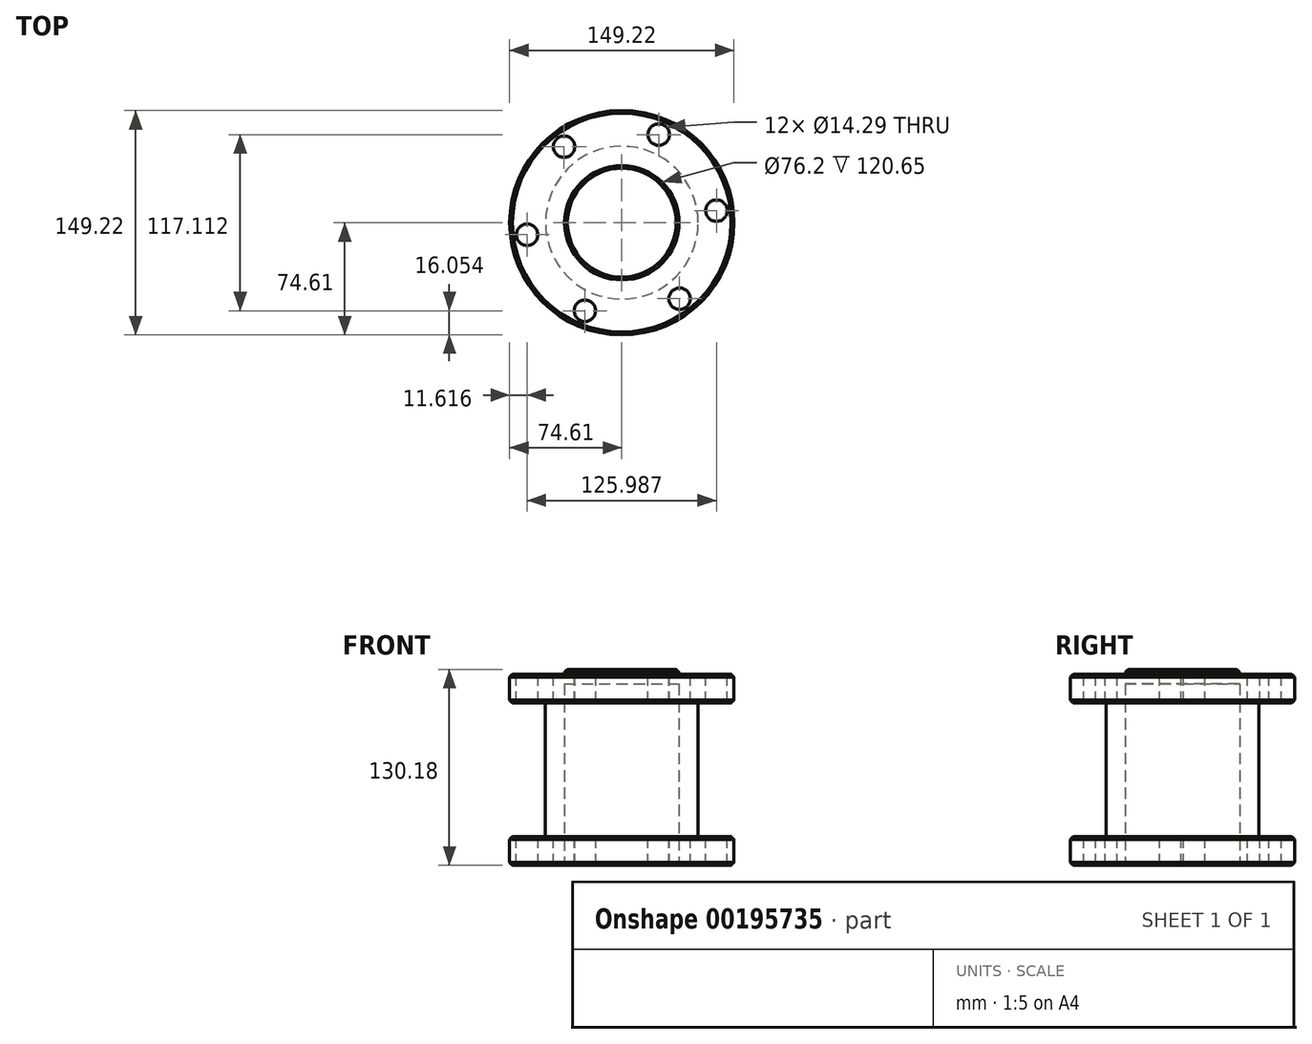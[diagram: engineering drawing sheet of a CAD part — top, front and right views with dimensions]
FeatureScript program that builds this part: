
annotation { "Feature Type Name" : "Feature", "Feature Type Description" : "" }
export const myFeature = defineFeature(function(context is Context, id is Id, definition is map)
    precondition{}
    {
        {
            var Q0;
            Q0=qCreatedBy(makeId("Top.planeOp"),FACE);
            var sketch = newSketch(context, id + "F0", { "sketchPlane" : qUnion([Q0])});
            skCircle(sketch, "E0", {"center": v(0, 0) * mm, "radius": 74.61 * mm});
            skSolve(sketch);
        }
        {
            var Q0;
            Q0 = qSketchRegion(id + "F0", true);
            extrude(context, id + "F1", {"entities" : qUnion([Q0]), "depth" : 19.05 * mm, "offsetDistance" : 25.4 * mm});
        }
        {
            var Q0;
            Q0=makeQuery(id+"F1.opExtrude","CAP_FACE",FACE,{"disambiguationData":[OSD([sQuery(id+"F0.wireOp",EDGE,"E0")])],"isStart":false});
            var sketch = newSketch(context, id + "F2", { "sketchPlane" : qUnion([Q0])});
            skCircle(sketch, "E1", {"center": v(0, 0) * mm, "radius": 50.8 * mm});
            skSolve(sketch);
        }
        {
            var Q0;
            Q0 = qSketchRegion(id + "F2", true);
            extrude(context, id + "F3", {"entities" : qUnion([Q0]), "operationType" : NewBodyOperationType.ADD, "depth" : 88.9 * mm, "offsetDistance" : 25.4 * mm});
        }
        {
            var Q0;
            Q0=makeQuery(id+"F3.opExtrude","CAP_FACE",FACE,{"disambiguationData":[OSD([sQuery(id+"F2.wireOp",EDGE,"E1")])],"isStart":false});
            var sketch = newSketch(context, id + "F4", { "sketchPlane" : qUnion([Q0])});
            skCircle(sketch, "E2", {"center": v(0, 0) * mm, "radius": 74.61 * mm});
            skSolve(sketch);
        }
        {
            var Q0;
            Q0 = qSketchRegion(id + "F4", true);
            extrude(context, id + "F5", {"entities" : qUnion([Q0]), "operationType" : NewBodyOperationType.ADD, "depth" : 19.05 * mm, "offsetDistance" : 25.4 * mm});
        }
        {
            var Q0;
            Q0=makeQuery(id+"F5.opExtrude","CAP_FACE",FACE,{"disambiguationData":[OSD([sQuery(id+"F4.wireOp",EDGE,"E2")])],"isStart":false});
            var sketch = newSketch(context, id + "F6", { "sketchPlane" : qUnion([Q0])});
            skCircle(sketch, "E3", {"center": v(0, 0) * mm, "radius": 63.5 * mm, "construction": true});
            skCircle(sketch, "E4", {"center": v(24.57, 58.56) * mm, "radius": 7.14 * mm});
            skCircle(sketch, "E5.1.0", {"center": v(-38.43, 50.55) * mm, "radius": 7.14 * mm});
            skCircle(sketch, "E5.2.0", {"center": v(-63, -8) * mm, "radius": 7.14 * mm});
            skCircle(sketch, "E5.3.0", {"center": v(-24.57, -58.56) * mm, "radius": 7.14 * mm});
            skCircle(sketch, "E5.4.0", {"center": v(38.43, -50.55) * mm, "radius": 7.14 * mm});
            skCircle(sketch, "E5.5.0", {"center": v(63, 8) * mm, "radius": 7.14 * mm});
            skSolve(sketch);
        }
        {
            var Q0;
            Q0 = qSketchRegion(id + "F6", true);
            extrude(context, id + "F7", {"entities" : qUnion([Q0]), "operationType" : NewBodyOperationType.REMOVE, "endBound" : BoundingType.THROUGH_ALL, "oppositeDirection" : true, "depth" : 25.4 * mm, "offsetDistance" : 25.4 * mm});
        }
        {
            var Q0;
            Q0=makeQuery(id+"F5.opExtrude","CAP_FACE",FACE,{"disambiguationData":[OSD([sQuery(id+"F4.wireOp",EDGE,"E2")])],"isStart":false});
            var sketch = newSketch(context, id + "F8", { "sketchPlane" : qUnion([Q0])});
            skCircle(sketch, "E6", {"center": v(0, 0) * mm, "radius": 38.1 * mm});
            skSolve(sketch);
        }
        {
            var Q0;
            Q0 = qSketchRegion(id + "F8", true);
            extrude(context, id + "F9", {"entities" : qUnion([Q0]), "operationType" : NewBodyOperationType.ADD, "depth" : 3.17 * mm, "offsetDistance" : 25.4 * mm});
        }
        {
            var Q0;
            Q0=makeQuery(id+"F1.opExtrude","CAP_FACE",FACE,{"disambiguationData":[OSD([sQuery(id+"F0.wireOp",EDGE,"E0")])],"isStart":true});
            var sketch = newSketch(context, id + "F10", { "sketchPlane" : qUnion([Q0])});
            skCircle(sketch, "E7", {"center": v(0, 0) * mm, "radius": 38.1 * mm});
            skSolve(sketch);
        }
        {
            var Q0;
            Q0 = qSketchRegion(id + "F10", true);
            extrude(context, id + "F11", {"entities" : qUnion([Q0]), "operationType" : NewBodyOperationType.REMOVE, "oppositeDirection" : true, "depth" : 120.65 * mm, "offsetDistance" : 25.4 * mm});
        }
        {
            var Q0;
            Q0=makeQuery(id+"F1.opExtrude","CAP_EDGE",EDGE,{"disambiguationData":[OSD([sQuery(id+"F0.wireOp",EDGE,"E0")])],"isStart":true});
            var Q1;
            Q1=makeQuery(id+"F11.boolean.opBoolean","COPY",EDGE,{"derivedFrom":makeQuery(id+"F11.opExtrude","CAP_EDGE",EDGE,{"disambiguationData":[OSD([sQuery(id+"F10.wireOp",EDGE,"E7")])],"isStart":true})});
            var Q2;
            Q2=makeQuery(id+"F1.opExtrude","CAP_EDGE",EDGE,{"disambiguationData":[OSD([sQuery(id+"F0.wireOp",EDGE,"E0")])],"isStart":false});
            var Q3;
            Q3=makeQuery(id+"F5.opExtrude","CAP_EDGE",EDGE,{"disambiguationData":[OSD([sQuery(id+"F4.wireOp",EDGE,"E2")])],"isStart":true});
            var Q4;
            Q4=makeQuery(id+"F5.opExtrude","CAP_EDGE",EDGE,{"disambiguationData":[OSD([sQuery(id+"F4.wireOp",EDGE,"E2")])],"isStart":false});
            var Q5;
            Q5=makeQuery(id+"F9.opExtrude","CAP_EDGE",EDGE,{"disambiguationData":[OSD([sQuery(id+"F8.wireOp",EDGE,"E6")])],"isStart":false});
            chamfer(context, id + "F12", {"entities" : qUnion([Q0, Q1, Q2, Q3, Q4, Q5]), "width" : 1.9 * mm, "tangentPropagation" : true});
        }
    });
